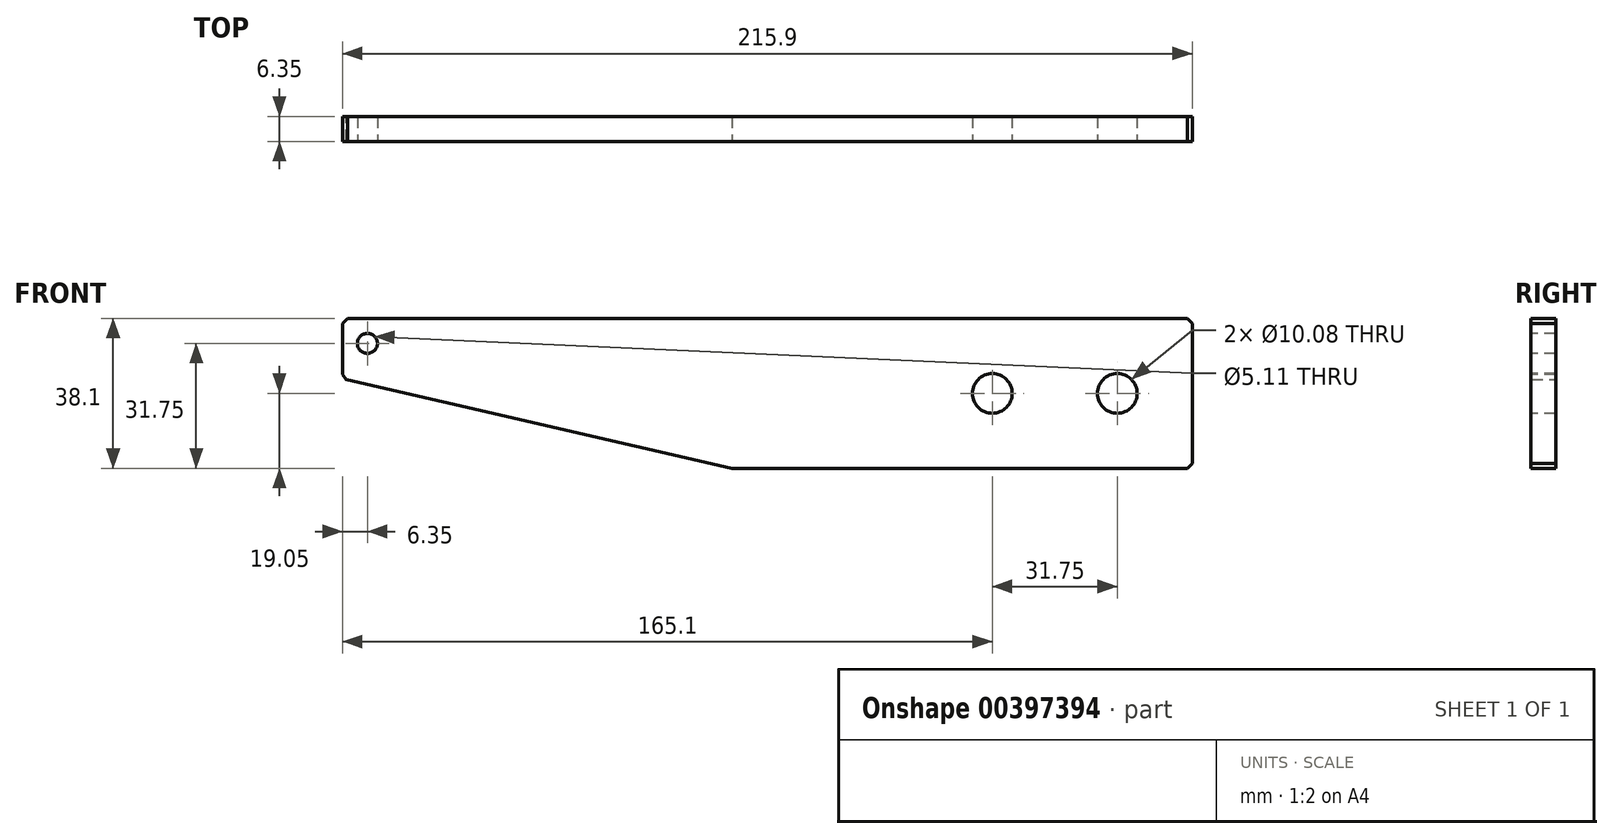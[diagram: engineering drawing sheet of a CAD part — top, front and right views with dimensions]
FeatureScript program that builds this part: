
annotation { "Feature Type Name" : "Feature", "Feature Type Description" : "" }
export const myFeature = defineFeature(function(context is Context, id is Id, definition is map)
    precondition{}
    {
        {
            var Q0;
            Q0=qCreatedBy(makeId("Front.planeOp"),FACE);
            var sketch = newSketch(context, id + "F0", { "sketchPlane" : qUnion([Q0])});
            skLineSegment(sketch, "E0", {"start": v(0, 0) * mm, "end": v(-215.9, 0) * mm});
            skLineSegment(sketch, "E1", {"start": v(-215.9, 0) * mm, "end": v(-215.9, -15.24) * mm});
            skLineSegment(sketch, "E2", {"start": v(-116.88, -38.1) * mm, "end": v(0, -38.1) * mm});
            skLineSegment(sketch, "E3", {"start": v(0, -38.1) * mm, "end": v(0, 0) * mm});
            skLineSegment(sketch, "E4.0", {"start": v(-215.9, -15.24) * mm, "end": v(-116.88, -38.1) * mm});
            skSolve(sketch);
        }
        {
            var Q0;
            Q0=makeQuery(id+"F0.imprint","IMPRINT",FACE,{"disambiguationData":[TD([[makeQuery(id+"F0.imprint","IMPRINT",EDGE,{"derivedFrom":sQuery(id+"F0.wireOp",EDGE,"E0")}),1.0]])]});
            extrude(context, id + "F1", {"entities" : qUnion([Q0]), "oppositeDirection" : true, "depth" : 6.35 * mm, "offsetDistance" : 25.4 * mm});
        }
        {
            var Q0;
            Q0=makeQuery(id+"F1.opExtrude","SWEPT_EDGE",EDGE,{"disambiguationData":[OSD([sQuery(id+"F0.wireOp",EDGE,"E0"),sQuery(id+"F0.wireOp",EDGE,"E1")])]});
            var Q1;
            Q1=makeQuery(id+"F1.opExtrude","SWEPT_EDGE",EDGE,{"disambiguationData":[OSD([sQuery(id+"F0.wireOp",EDGE,"E1"),sQuery(id+"F0.wireOp",EDGE,"34DIQ4tQ-PNsC-aAL2-XCtS-DoHARtBsPdQU")])]});
            var Q2;
            Q2=makeQuery(id+"F1.opExtrude","SWEPT_EDGE",EDGE,{"disambiguationData":[OSD([sQuery(id+"F0.wireOp",EDGE,"E2"),sQuery(id+"F0.wireOp",EDGE,"E3")])]});
            var Q3;
            Q3=makeQuery(id+"F1.opExtrude","SWEPT_EDGE",EDGE,{"disambiguationData":[OSD([sQuery(id+"F0.wireOp",EDGE,"E0"),sQuery(id+"F0.wireOp",EDGE,"E3")])]});
            chamfer(context, id + "F2", {"entities" : qUnion([Q0, Q1, Q2, Q3]), "width" : 1.27 * mm, "tangentPropagation" : true});
        }
        {
            var Q0;
            Q0=makeQuery(id+"F1.opExtrude","CAP_FACE",FACE,{"disambiguationData":[OSD([sQuery(id+"F0.wireOp",EDGE,"E0"),sQuery(id+"F0.wireOp",EDGE,"E1"),sQuery(id+"F0.wireOp",EDGE,"E2"),sQuery(id+"F0.wireOp",EDGE,"E3"),sQuery(id+"F0.wireOp",EDGE,"E4.0")])],"isStart":true});
            var sketch = newSketch(context, id + "F3", { "sketchPlane" : qUnion([Q0])});
            skCircle(sketch, "E5", {"center": v(-19.05, -19.05) * mm, "radius": 4.76 * mm});
            skCircle(sketch, "E6", {"center": v(-50.8, -19.05) * mm, "radius": 4.76 * mm});
            skSolve(sketch);
        }
        {
            var Q0;
            Q0=sQuery(id+"F3.wireOp",VERTEX,"E6.center");
            var Q1;
            Q1=sQuery(id+"F3.wireOp",VERTEX,"E5.center");
            var Q2;
            Q2=makeQuery(id+"F1.opExtrude","SWEPT_BODY",BODY,{"disambiguationData":[OSD([sQuery(id+"F0.wireOp",EDGE,"E0"),sQuery(id+"F0.wireOp",EDGE,"E1"),sQuery(id+"F0.wireOp",EDGE,"E2"),sQuery(id+"F0.wireOp",EDGE,"E3"),sQuery(id+"F0.wireOp",EDGE,"E4.0")])]});
            hole(context, id + "F4", {"style" : HoleStyle.SIMPLE, "endStyle" : HoleEndStyle.THROUGH, "standardTappedOrClearance" : lookupTablePath({ "standard" : "ANSI", "fit" : "Normal (ASME)", "size" : "3/8", "type" : "Clearance" }), "standardBlindInLast" : lookupTablePath({ "fit" : "Free", "standard" : "ANSI", "size" : "3/8", "type" : "Clearance" }), "holeDiameter" : 10.08 * mm, "majorDiameter" : 12.7 * mm, "isTappedThrough" : true, "tappedDepth" : 12.73 * mm, "tapClearance" : 3, "locations" : qUnion([Q0, Q1]), "scope" : qUnion([Q2])});
        }
        {
            var Q0;
            Q0=makeQuery(id+"F1.opExtrude","CAP_FACE",FACE,{"disambiguationData":[OSD([sQuery(id+"F0.wireOp",EDGE,"E0"),sQuery(id+"F0.wireOp",EDGE,"E1"),sQuery(id+"F0.wireOp",EDGE,"E2"),sQuery(id+"F0.wireOp",EDGE,"E3"),sQuery(id+"F0.wireOp",EDGE,"E4.0")])],"isStart":true});
            var sketch = newSketch(context, id + "F5", { "sketchPlane" : qUnion([Q0])});
            skCircle(sketch, "E7", {"center": v(-209.55, -6.35) * mm, "radius": 2.54 * mm});
            skSolve(sketch);
        }
        {
            var Q0;
            Q0=sQuery(id+"F5.wireOp",VERTEX,"E7.center");
            var Q1;
            Q1=makeQuery(id+"F1.opExtrude","SWEPT_BODY",BODY,{"disambiguationData":[OSD([sQuery(id+"F0.wireOp",EDGE,"E0"),sQuery(id+"F0.wireOp",EDGE,"E1"),sQuery(id+"F0.wireOp",EDGE,"E2"),sQuery(id+"F0.wireOp",EDGE,"E3"),sQuery(id+"F0.wireOp",EDGE,"E4.0")])]});
            hole(context, id + "F6", {"style" : HoleStyle.SIMPLE, "endStyle" : HoleEndStyle.THROUGH, "standardTappedOrClearance" : lookupTablePath({ "standard" : "ANSI", "engagement" : "75%", "pitch" : "20 tpi", "size" : "1/4", "type" : "Tapped" }), "standardBlindInLast" : lookupTablePath({ "standard" : "ANSI", "engagement" : "75%", "pitch" : "20 tpi", "size" : "1/4", "type" : "Tapped" }), "holeDiameter" : 5.1 * mm, "majorDiameter" : 6.35 * mm, "showTappedDepth" : true, "isTappedThrough" : true, "tappedDepth" : 12.73 * mm, "tapClearance" : 3, "locations" : qUnion([Q0]), "scope" : qUnion([Q1])});
        }
    });
